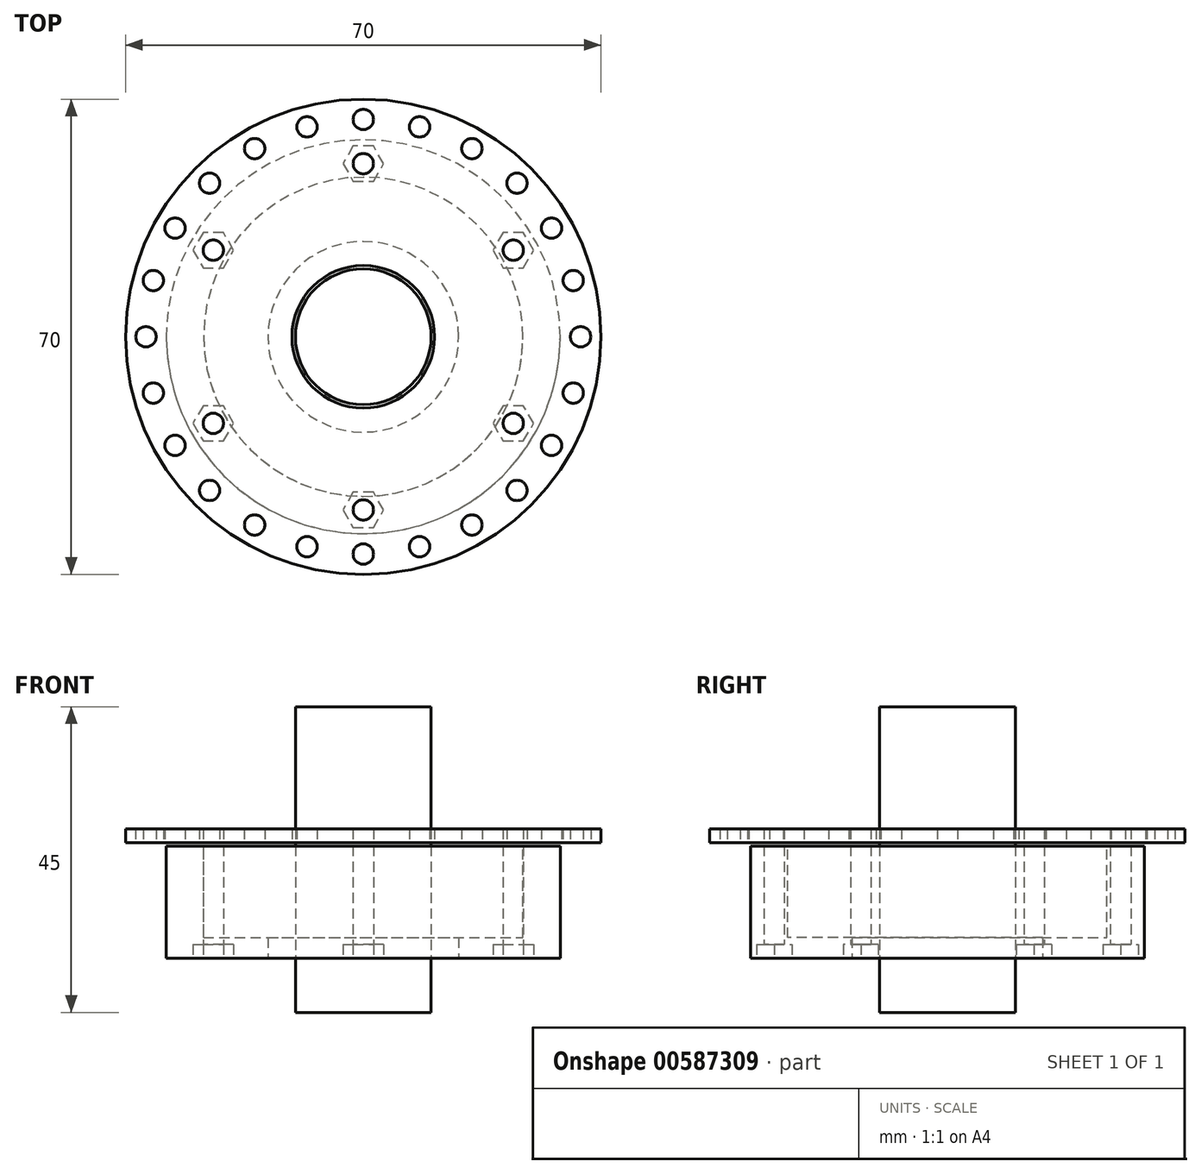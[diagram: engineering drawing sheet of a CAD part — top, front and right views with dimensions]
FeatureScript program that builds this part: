
annotation { "Feature Type Name" : "Feature", "Feature Type Description" : "" }
export const myFeature = defineFeature(function(context is Context, id is Id, definition is map)
    precondition{}
    {
        {
            var Q0;
            Q0=qCreatedBy(makeId("Top.planeOp"),FACE);
            var sketch = newSketch(context, id + "F0", { "sketchPlane" : qUnion([Q0]) });
            skCircle(sketch, "E0", {"center": v(0, 0) * mm, "radius": 10 * mm});
            skCircle(sketch, "E1", {"center": v(0, 0) * mm, "radius": 23.5 * mm});
            skCircle(sketch, "E2", {"center": v(0, 0) * mm, "radius": 19.54 * mm});
            skCircle(sketch, "E3", {"center": v(0, 0) * mm, "radius": 14.04 * mm});
            skSolve(sketch);
        }
        {
            var Q0;
            Q0=makeQuery(id+"F0.imprint","IMPRINT",FACE,{"disambiguationData":[TD([[makeQuery(id+"F0.imprint","IMPRINT",EDGE,{"derivedFrom":sQuery(id+"F0.wireOp",EDGE,"E2")}),1.0]])]});
            var Q1;
            Q1=makeQuery(id+"F0.imprint","IMPRINT",FACE,{"disambiguationData":[TD([[makeQuery(id+"F0.imprint","IMPRINT",EDGE,{"derivedFrom":sQuery(id+"F0.wireOp",EDGE,"E1")}),1.0]])]});
            var Q2;
            Q2=makeQuery(id+"F0.imprint","IMPRINT",FACE,{"disambiguationData":[TD([[makeQuery(id+"F0.imprint","IMPRINT",EDGE,{"derivedFrom":sQuery(id+"F0.wireOp",EDGE,"E0")}),-1.0]])]});
            extrude(context, id + "F1", {"entities" : qUnion([Q0, Q1, Q2]), "oppositeDirection" : true, "depth" : 14 * mm, "offsetDistance" : 25 * mm});
        }
        {
            var Q0;
            Q0=makeQuery(id+"F0.imprint","IMPRINT",FACE,{"disambiguationData":[TD([[makeQuery(id+"F0.imprint","IMPRINT",EDGE,{"derivedFrom":sQuery(id+"F0.wireOp",EDGE,"E2")}),1.0]])]});
            extrude(context, id + "F2", {"entities" : qUnion([Q0]), "operationType" : NewBodyOperationType.REMOVE, "oppositeDirection" : true, "depth" : 2 * mm, "offsetDistance" : 25 * mm});
        }
        {
            var Q0;
            Q0=makeQuery(id+"F1.opExtrude","CAP_EDGE",EDGE,{"disambiguationData":[OSD([sQuery(id+"F0.wireOp",EDGE,"E1")])],"isStart":true});
            var Q1;
            Q1=makeQuery(id+"F1.opExtrude","CAP_EDGE",EDGE,{"disambiguationData":[OSD([sQuery(id+"F0.wireOp",EDGE,"E1")])],"isStart":false});
            chamfer(context, id + "F3", {"entities" : qUnion([Q0, Q1]), "width" : 2 * mm, "tangentPropagation" : true});
        }
        {
            var Q0;
            Q0=makeQuery(id+"F1.opExtrude","CAP_EDGE",EDGE,{"disambiguationData":[OSD([sQuery(id+"F0.wireOp",EDGE,"E0")])],"isStart":false});
            var Q1;
            Q1=makeQuery(id+"F1.opExtrude","CAP_EDGE",EDGE,{"disambiguationData":[OSD([sQuery(id+"F0.wireOp",EDGE,"E0")])],"isStart":true});
            chamfer(context, id + "F4", {"entities" : qUnion([Q0, Q1]), "width" : 1 * mm, "tangentPropagation" : true});
        }
        {
            var Q0;
            Q0=makeQuery(id+"F1.opExtrude","CAP_FACE",FACE,{"disambiguationData":[OSD([sQuery(id+"F0.wireOp",EDGE,"E0"),sQuery(id+"F0.wireOp",EDGE,"E1")])],"isStart":false});
            var sketch = newSketch(context, id + "F5", { "sketchPlane" : qUnion([Q0]) });
            skCircle(sketch, "E4.0", {"center": v(0, 0) * mm, "radius": 14.04 * mm});
            skCircle(sketch, "E5.0", {"center": v(0, 0) * mm, "radius": 19.54 * mm});
            skSolve(sketch);
        }
        {
            var Q0;
            Q0 = qSketchRegion(id + "F5", true);
            extrude(context, id + "F6", {"entities" : qUnion([Q0]), "operationType" : NewBodyOperationType.REMOVE, "oppositeDirection" : true, "depth" : 2 * mm, "offsetDistance" : 25 * mm});
        }
        {
            var Q0;
            Q0=qCreatedBy(makeId("Top.planeOp"),FACE);
            var sketch = newSketch(context, id + "F7", { "sketchPlane" : qUnion([Q0]) });
            skCircle(sketch, "E6", {"center": v(0, 0) * mm, "radius": 35 * mm});
            skCircle(sketch, "E7", {"center": v(0, 32) * mm, "radius": 1.5 * mm});
            skCircle(sketch, "E8.1.0", {"center": v(-8.28, 30.9) * mm, "radius": 1.5 * mm});
            skCircle(sketch, "E8.2.0", {"center": v(-16, 27.71) * mm, "radius": 1.5 * mm});
            skCircle(sketch, "E8.3.0", {"center": v(-22.63, 22.63) * mm, "radius": 1.5 * mm});
            skCircle(sketch, "E8.4.0", {"center": v(-27.71, 16) * mm, "radius": 1.5 * mm});
            skCircle(sketch, "E8.5.0", {"center": v(-30.9, 8.28) * mm, "radius": 1.5 * mm});
            skCircle(sketch, "E8.6.0", {"center": v(-32, 0) * mm, "radius": 1.5 * mm});
            skCircle(sketch, "E8.7.0", {"center": v(-30.9, -8.28) * mm, "radius": 1.5 * mm});
            skCircle(sketch, "E8.8.0", {"center": v(-27.71, -16) * mm, "radius": 1.5 * mm});
            skCircle(sketch, "E8.9.0", {"center": v(-22.63, -22.63) * mm, "radius": 1.5 * mm});
            skCircle(sketch, "E8.10.0", {"center": v(-16, -27.71) * mm, "radius": 1.5 * mm});
            skCircle(sketch, "E8.11.0", {"center": v(-8.28, -30.9) * mm, "radius": 1.5 * mm});
            skCircle(sketch, "E8.12.0", {"center": v(0, -32) * mm, "radius": 1.5 * mm});
            skCircle(sketch, "E8.13.0", {"center": v(8.28, -30.9) * mm, "radius": 1.5 * mm});
            skCircle(sketch, "E8.14.0", {"center": v(16, -27.71) * mm, "radius": 1.5 * mm});
            skCircle(sketch, "E8.15.0", {"center": v(22.63, -22.63) * mm, "radius": 1.5 * mm});
            skCircle(sketch, "E8.16.0", {"center": v(27.71, -16) * mm, "radius": 1.5 * mm});
            skCircle(sketch, "E8.17.0", {"center": v(30.9, -8.28) * mm, "radius": 1.5 * mm});
            skCircle(sketch, "E8.18.0", {"center": v(32, 0) * mm, "radius": 1.5 * mm});
            skCircle(sketch, "E8.19.0", {"center": v(30.9, 8.28) * mm, "radius": 1.5 * mm});
            skCircle(sketch, "E8.20.0", {"center": v(27.71, 16) * mm, "radius": 1.5 * mm});
            skCircle(sketch, "E8.21.0", {"center": v(22.63, 22.63) * mm, "radius": 1.5 * mm});
            skCircle(sketch, "E8.22.0", {"center": v(16, 27.71) * mm, "radius": 1.5 * mm});
            skCircle(sketch, "E8.23.0", {"center": v(8.28, 30.9) * mm, "radius": 1.5 * mm});
            skCircle(sketch, "E9", {"center": v(0, 0) * mm, "radius": 10.5 * mm});
            skSolve(sketch);
        }
        {
            var Q0;
            Q0=makeQuery(id+"F7.imprint","IMPRINT",FACE,{"disambiguationData":[TD([[makeQuery(id+"F7.imprint","IMPRINT",EDGE,{"derivedFrom":sQuery(id+"F7.wireOp",EDGE,"E6")}),1.0]])]});
            extrude(context, id + "F8", {"entities" : qUnion([Q0]), "depth" : 2 * mm, "offsetDistance" : 25 * mm});
        }
        {
            var Q0;
            {var subQ0=sQuery(id+"F0.wireOp",EDGE,"E0");Q0=makeQuery(id+"F6.boolean.opBoolean","SPLIT",FACE,{"disambiguationData":[TD([makeQuery(id+"F6.opExtrude","SWEPT_FACE",FACE,{"disambiguationData":[OSD([sQuery(id+"F5.wireOp",EDGE,"E4.0")])]})])],"derivedFrom":makeQuery(id+"F1.opExtrude","CAP_FACE",FACE,{"disambiguationData":[OSD([subQ0,sQuery(id+"F0.wireOp",EDGE,"E1")])],"isStart":false})});}
            var sketch = newSketch(context, id + "F9", { "sketchPlane" : qUnion([Q0]) });
            skCircle(sketch, "E10", {"center": v(0, 0) * mm, "radius": 29 * mm});
            skCircle(sketch, "E11.0", {"center": v(0, 0) * mm, "radius": 10 * mm, "construction": true});
            skCircle(sketch, "E12", {"center": v(0, 0) * mm, "radius": 10.5 * mm});
            skSolve(sketch);
        }
        {
            var Q0;
            Q0=makeQuery(id+"F9.imprint","IMPRINT",FACE,{"disambiguationData":[TD([[makeQuery(id+"F9.imprint","IMPRINT",EDGE,{"derivedFrom":makeQuery(id+"F6.boolean.opBoolean","COPY",EDGE,{"derivedFrom":makeQuery(id+"F6.opExtrude","CAP_EDGE",EDGE,{"disambiguationData":[OSD([sQuery(id+"F5.wireOp",EDGE,"E4.0")])],"isStart":true})})}),-1.0]])]});
            var Q1;
            Q1=makeQuery(id+"F9.imprint","IMPRINT",FACE,{"disambiguationData":[TD([[makeQuery(id+"F9.imprint","IMPRINT",EDGE,{"derivedFrom":sQuery(id+"F9.wireOp",EDGE,"E10")}),1.0]])]});
            var Q2;
            Q2=makeQuery(id+"F8.opExtrude","CAP_FACE",FACE,{"disambiguationData":[OSD([sQuery(id+"F7.wireOp",EDGE,"E6"),sQuery(id+"F7.wireOp",EDGE,"E7"),sQuery(id+"F7.wireOp",EDGE,"E8.1.0"),sQuery(id+"F7.wireOp",EDGE,"E8.2.0"),sQuery(id+"F7.wireOp",EDGE,"E8.3.0"),sQuery(id+"F7.wireOp",EDGE,"E8.4.0"),sQuery(id+"F7.wireOp",EDGE,"E8.5.0"),sQuery(id+"F7.wireOp",EDGE,"E8.6.0"),sQuery(id+"F7.wireOp",EDGE,"E8.7.0"),sQuery(id+"F7.wireOp",EDGE,"E8.8.0"),sQuery(id+"F7.wireOp",EDGE,"E8.9.0"),sQuery(id+"F7.wireOp",EDGE,"E8.10.0"),sQuery(id+"F7.wireOp",EDGE,"E8.11.0"),sQuery(id+"F7.wireOp",EDGE,"E8.12.0"),sQuery(id+"F7.wireOp",EDGE,"E8.13.0"),sQuery(id+"F7.wireOp",EDGE,"E8.14.0"),sQuery(id+"F7.wireOp",EDGE,"E8.15.0"),sQuery(id+"F7.wireOp",EDGE,"E8.16.0"),sQuery(id+"F7.wireOp",EDGE,"E8.17.0"),sQuery(id+"F7.wireOp",EDGE,"E8.18.0"),sQuery(id+"F7.wireOp",EDGE,"E8.19.0"),sQuery(id+"F7.wireOp",EDGE,"E8.20.0"),sQuery(id+"F7.wireOp",EDGE,"E8.21.0"),sQuery(id+"F7.wireOp",EDGE,"E8.22.0"),sQuery(id+"F7.wireOp",EDGE,"E8.23.0"),sQuery(id+"F7.wireOp",EDGE,"E9"),sQuery(id+"F7.wireOp",EDGE,"SUpEN3Z2-evRc-ZjCU-vPrQ-KYs7HBq4r9Lc"),sQuery(id+"F7.wireOp",EDGE,"4f132e4c-be19-42d6-8573-d693d6a31837.1.0"),sQuery(id+"F7.wireOp",EDGE,"4f132e4c-be19-42d6-8573-d693d6a31837.2.0"),sQuery(id+"F7.wireOp",EDGE,"4f132e4c-be19-42d6-8573-d693d6a31837.3.0")])],"isStart":true});
            var Q3;
            Q3=makeQuery(id+"F8.opExtrude","SWEPT_BODY",BODY,{"disambiguationData":[OSD([sQuery(id+"F7.wireOp",EDGE,"E6"),sQuery(id+"F7.wireOp",EDGE,"E7"),sQuery(id+"F7.wireOp",EDGE,"E8.1.0"),sQuery(id+"F7.wireOp",EDGE,"E8.2.0"),sQuery(id+"F7.wireOp",EDGE,"E8.3.0"),sQuery(id+"F7.wireOp",EDGE,"E8.4.0"),sQuery(id+"F7.wireOp",EDGE,"E8.5.0"),sQuery(id+"F7.wireOp",EDGE,"E8.6.0"),sQuery(id+"F7.wireOp",EDGE,"E8.7.0"),sQuery(id+"F7.wireOp",EDGE,"E8.8.0"),sQuery(id+"F7.wireOp",EDGE,"E8.9.0"),sQuery(id+"F7.wireOp",EDGE,"E8.10.0"),sQuery(id+"F7.wireOp",EDGE,"E8.11.0"),sQuery(id+"F7.wireOp",EDGE,"E8.12.0"),sQuery(id+"F7.wireOp",EDGE,"E8.13.0"),sQuery(id+"F7.wireOp",EDGE,"E8.14.0"),sQuery(id+"F7.wireOp",EDGE,"E8.15.0"),sQuery(id+"F7.wireOp",EDGE,"E8.16.0"),sQuery(id+"F7.wireOp",EDGE,"E8.17.0"),sQuery(id+"F7.wireOp",EDGE,"E8.18.0"),sQuery(id+"F7.wireOp",EDGE,"E8.19.0"),sQuery(id+"F7.wireOp",EDGE,"E8.20.0"),sQuery(id+"F7.wireOp",EDGE,"E8.21.0"),sQuery(id+"F7.wireOp",EDGE,"E8.22.0"),sQuery(id+"F7.wireOp",EDGE,"E8.23.0"),sQuery(id+"F7.wireOp",EDGE,"E9"),sQuery(id+"F7.wireOp",EDGE,"SUpEN3Z2-evRc-ZjCU-vPrQ-KYs7HBq4r9Lc"),sQuery(id+"F7.wireOp",EDGE,"4f132e4c-be19-42d6-8573-d693d6a31837.1.0"),sQuery(id+"F7.wireOp",EDGE,"4f132e4c-be19-42d6-8573-d693d6a31837.2.0"),sQuery(id+"F7.wireOp",EDGE,"4f132e4c-be19-42d6-8573-d693d6a31837.3.0")])]});
            extrude(context, id + "F10", {"entities" : qUnion([Q0, Q1]), "endBound" : BoundingType.UP_TO_SURFACE, "oppositeDirection" : true, "depth" : 25 * mm, "endBoundEntityFace" : qUnion([Q2]), "endBoundEntityBody" : qUnion([Q3]), "hasOffset" : true, "offsetDistance" : 0.5 * mm, "hasSecondDirection" : true, "secondDirectionOppositeDirection" : false, "secondDirectionDepth" : 3 * mm});
        }
        {
            var Q0;
            Q0=makeQuery(id+"F0.imprint","IMPRINT",FACE,{"disambiguationData":[TD([[makeQuery(id+"F0.imprint","IMPRINT",EDGE,{"derivedFrom":sQuery(id+"F0.wireOp",EDGE,"E0")}),-1.0]])]});
            var Q1;
            Q1=makeQuery(id+"F0.imprint","IMPRINT",FACE,{"disambiguationData":[TD([[makeQuery(id+"F0.imprint","IMPRINT",EDGE,{"derivedFrom":sQuery(id+"F0.wireOp",EDGE,"E2")}),1.0]])]});
            var Q2;
            Q2=makeQuery(id+"F0.imprint","IMPRINT",FACE,{"disambiguationData":[TD([[makeQuery(id+"F0.imprint","IMPRINT",EDGE,{"derivedFrom":sQuery(id+"F0.wireOp",EDGE,"E1")}),1.0]])]});
            var Q3;
            Q3=makeQuery(id+"F10.opExtrude","CAP_FACE",FACE,{"disambiguationData":[OSD([sQuery(id+"F0.wireOp",EDGE,"E0"),sQuery(id+"F0.wireOp",EDGE,"E1"),sQuery(id+"F9.wireOp",EDGE,"E10")])],"isStart":true});
            extrude(context, id + "F11", {"entities" : qUnion([Q0, Q1, Q2]), "operationType" : NewBodyOperationType.REMOVE, "endBound" : BoundingType.UP_TO_SURFACE, "oppositeDirection" : true, "depth" : 25 * mm, "endBoundEntityFace" : qUnion([Q3]), "hasOffset" : true, "offsetDistance" : 3 * mm});
        }
        {
            var Q0;
            Q0=makeQuery(id+"F0.imprint","IMPRINT",FACE,{"disambiguationData":[TD([[makeQuery(id+"F0.imprint","IMPRINT",EDGE,{"derivedFrom":sQuery(id+"F0.wireOp",EDGE,"E0")}),1.0]])]});
            extrude(context, id + "F12", {"entities" : qUnion([Q0]), "depth" : 20 * mm, "offsetDistance" : 25 * mm, "hasSecondDirection" : true, "secondDirectionOppositeDirection" : true, "secondDirectionDepth" : 25 * mm});
        }
        {
            var Q0;
            Q0=makeQuery(id+"F10.opExtrude","CAP_FACE",FACE,{"disambiguationData":[OSD([sQuery(id+"F0.wireOp",EDGE,"E0"),sQuery(id+"F0.wireOp",EDGE,"E1"),sQuery(id+"F9.wireOp",EDGE,"E10")])],"isStart":true});
            var sketch = newSketch(context, id + "F13", { "sketchPlane" : qUnion([Q0]) });
            skCircle(sketch, "E13", {"center": v(0, 25.5) * mm, "radius": 1.5 * mm});
            skCircle(sketch, "E14.1.0", {"center": v(-22.08, 12.75) * mm, "radius": 1.5 * mm});
            skCircle(sketch, "E14.2.0", {"center": v(-22.08, -12.75) * mm, "radius": 1.5 * mm});
            skCircle(sketch, "E14.3.0", {"center": v(0, -25.5) * mm, "radius": 1.5 * mm});
            skPoint(sketch, "E14.center", {"position": v(0, 0) * mm});
            skCircle(sketch, "E15.0", {"center": v(0, 0) * mm, "radius": 23.5 * mm, "construction": true});
            skCircle(sketch, "E16.1.4.0", {"center": v(22.08, -12.75) * mm, "radius": 1.5 * mm});
            skCircle(sketch, "E16.1.5.0", {"center": v(22.08, 12.75) * mm, "radius": 1.5 * mm});
            skSolve(sketch);
        }
        {
            var Q0;
            Q0=makeQuery(id+"F13.imprint","IMPRINT",FACE,{"disambiguationData":[TD([[makeQuery(id+"F13.imprint","IMPRINT",EDGE,{"derivedFrom":sQuery(id+"F13.wireOp",EDGE,"E13")}),1.0]])]});
            var Q1;
            Q1=makeQuery(id+"F13.imprint","IMPRINT",FACE,{"disambiguationData":[TD([[makeQuery(id+"F13.imprint","IMPRINT",EDGE,{"derivedFrom":sQuery(id+"F13.wireOp",EDGE,"E14.1.0")}),1.0]])]});
            var Q2;
            Q2=makeQuery(id+"F13.imprint","IMPRINT",FACE,{"disambiguationData":[TD([[makeQuery(id+"F13.imprint","IMPRINT",EDGE,{"derivedFrom":sQuery(id+"F13.wireOp",EDGE,"E14.2.0")}),1.0]])]});
            var Q3;
            Q3=makeQuery(id+"F13.imprint","IMPRINT",FACE,{"disambiguationData":[TD([[makeQuery(id+"F13.imprint","IMPRINT",EDGE,{"derivedFrom":sQuery(id+"F13.wireOp",EDGE,"E14.3.0")}),1.0]])]});
            var Q4;
            Q4=makeQuery(id+"F13.imprint","IMPRINT",FACE,{"disambiguationData":[TD([[makeQuery(id+"F13.imprint","IMPRINT",EDGE,{"derivedFrom":sQuery(id+"F13.wireOp",EDGE,"E16.1.5.0")}),1.0]])]});
            var Q5;
            Q5=makeQuery(id+"F13.imprint","IMPRINT",FACE,{"disambiguationData":[TD([[makeQuery(id+"F13.imprint","IMPRINT",EDGE,{"derivedFrom":sQuery(id+"F13.wireOp",EDGE,"E16.1.4.0")}),1.0]])]});
            extrude(context, id + "F14", {"entities" : qUnion([Q0, Q1, Q2, Q3, Q4, Q5]), "operationType" : NewBodyOperationType.REMOVE, "endBound" : BoundingType.THROUGH_ALL, "oppositeDirection" : true, "depth" : 25 * mm, "offsetDistance" : 25 * mm});
        }
        {
            var Q0;
            Q0=makeQuery(id+"F10.opExtrude","CAP_FACE",FACE,{"disambiguationData":[OSD([sQuery(id+"F0.wireOp",EDGE,"E0"),sQuery(id+"F0.wireOp",EDGE,"E1"),sQuery(id+"F9.wireOp",EDGE,"E10")])],"isStart":true});
            var sketch = newSketch(context, id + "F15", { "sketchPlane" : qUnion([Q0]) });
            skCircle(sketch, "E17.cCircle", {"center": v(0, 25.5) * mm, "radius": 3 * mm, "construction": true});
            skLineSegment(sketch, "E17.0", {"start": v(1.5, 22.9) * mm, "end": v(-1.5, 22.9) * mm});
            skLineSegment(sketch, "E17.1", {"start": v(-1.5, 22.9) * mm, "end": v(-3, 25.5) * mm});
            skLineSegment(sketch, "E17.2", {"start": v(-3, 25.5) * mm, "end": v(-1.5, 28.1) * mm});
            skLineSegment(sketch, "E17.3", {"start": v(-1.5, 28.1) * mm, "end": v(1.5, 28.1) * mm});
            skLineSegment(sketch, "E17.4", {"start": v(1.5, 28.1) * mm, "end": v(3, 25.5) * mm});
            skLineSegment(sketch, "E17.5", {"start": v(3, 25.5) * mm, "end": v(1.5, 22.9) * mm});
            skLineSegment(sketch, "E18.1.0", {"start": v(-23.58, 10.15) * mm, "end": v(-25.08, 12.75) * mm});
            skLineSegment(sketch, "E18.1.1", {"start": v(-25.08, 12.75) * mm, "end": v(-23.58, 15.35) * mm});
            skLineSegment(sketch, "E18.1.2", {"start": v(-23.58, 15.35) * mm, "end": v(-20.58, 15.35) * mm});
            skLineSegment(sketch, "E18.1.3", {"start": v(-20.58, 15.35) * mm, "end": v(-19.08, 12.75) * mm});
            skLineSegment(sketch, "E18.1.4", {"start": v(-19.08, 12.75) * mm, "end": v(-20.58, 10.15) * mm});
            skLineSegment(sketch, "E18.1.5", {"start": v(-20.58, 10.15) * mm, "end": v(-23.58, 10.15) * mm});
            skLineSegment(sketch, "E18.2.0", {"start": v(-20.58, -15.35) * mm, "end": v(-23.58, -15.35) * mm});
            skLineSegment(sketch, "E18.2.1", {"start": v(-23.58, -15.35) * mm, "end": v(-25.08, -12.75) * mm});
            skLineSegment(sketch, "E18.2.2", {"start": v(-25.08, -12.75) * mm, "end": v(-23.58, -10.15) * mm});
            skLineSegment(sketch, "E18.2.3", {"start": v(-23.58, -10.15) * mm, "end": v(-20.58, -10.15) * mm});
            skLineSegment(sketch, "E18.2.4", {"start": v(-20.58, -10.15) * mm, "end": v(-19.08, -12.75) * mm});
            skLineSegment(sketch, "E18.2.5", {"start": v(-19.08, -12.75) * mm, "end": v(-20.58, -15.35) * mm});
            skLineSegment(sketch, "E18.3.0", {"start": v(3, -25.5) * mm, "end": v(1.5, -28.1) * mm});
            skLineSegment(sketch, "E18.3.1", {"start": v(1.5, -28.1) * mm, "end": v(-1.5, -28.1) * mm});
            skLineSegment(sketch, "E18.3.2", {"start": v(-1.5, -28.1) * mm, "end": v(-3, -25.5) * mm});
            skLineSegment(sketch, "E18.3.3", {"start": v(-3, -25.5) * mm, "end": v(-1.5, -22.9) * mm});
            skLineSegment(sketch, "E18.3.4", {"start": v(-1.5, -22.9) * mm, "end": v(1.5, -22.9) * mm});
            skLineSegment(sketch, "E18.3.5", {"start": v(1.5, -22.9) * mm, "end": v(3, -25.5) * mm});
            skLineSegment(sketch, "E18.4.0", {"start": v(23.58, -10.15) * mm, "end": v(25.08, -12.75) * mm});
            skLineSegment(sketch, "E18.4.1", {"start": v(25.08, -12.75) * mm, "end": v(23.58, -15.35) * mm});
            skLineSegment(sketch, "E18.4.2", {"start": v(23.58, -15.35) * mm, "end": v(20.58, -15.35) * mm});
            skLineSegment(sketch, "E18.4.3", {"start": v(20.58, -15.35) * mm, "end": v(19.08, -12.75) * mm});
            skLineSegment(sketch, "E18.4.4", {"start": v(19.08, -12.75) * mm, "end": v(20.58, -10.15) * mm});
            skLineSegment(sketch, "E18.4.5", {"start": v(20.58, -10.15) * mm, "end": v(23.58, -10.15) * mm});
            skLineSegment(sketch, "E18.5.0", {"start": v(20.58, 15.35) * mm, "end": v(23.58, 15.35) * mm});
            skLineSegment(sketch, "E18.5.1", {"start": v(23.58, 15.35) * mm, "end": v(25.08, 12.75) * mm});
            skLineSegment(sketch, "E18.5.2", {"start": v(25.08, 12.75) * mm, "end": v(23.58, 10.15) * mm});
            skLineSegment(sketch, "E18.5.3", {"start": v(23.58, 10.15) * mm, "end": v(20.58, 10.15) * mm});
            skLineSegment(sketch, "E18.5.4", {"start": v(20.58, 10.15) * mm, "end": v(19.08, 12.75) * mm});
            skLineSegment(sketch, "E18.5.5", {"start": v(19.08, 12.75) * mm, "end": v(20.58, 15.35) * mm});
            skPoint(sketch, "E18.center", {"position": v(0, 0) * mm});
            skSolve(sketch);
        }
        {
            var Q0;
            Q0=makeQuery(id+"F15.imprint","IMPRINT",FACE,{"disambiguationData":[TD([[makeQuery(id+"F15.imprint","IMPRINT",EDGE,{"derivedFrom":sQuery(id+"F15.wireOp",EDGE,"E17.0")}),-1.0]])]});
            var Q1;
            Q1=makeQuery(id+"F15.imprint","IMPRINT",FACE,{"disambiguationData":[TD([[makeQuery(id+"F15.imprint","IMPRINT",EDGE,{"derivedFrom":sQuery(id+"F15.wireOp",EDGE,"E18.1.0")}),-1.0]])]});
            var Q2;
            Q2=makeQuery(id+"F15.imprint","IMPRINT",FACE,{"disambiguationData":[TD([[makeQuery(id+"F15.imprint","IMPRINT",EDGE,{"derivedFrom":sQuery(id+"F15.wireOp",EDGE,"E18.2.0")}),-1.0]])]});
            var Q3;
            Q3=makeQuery(id+"F15.imprint","IMPRINT",FACE,{"disambiguationData":[TD([[makeQuery(id+"F15.imprint","IMPRINT",EDGE,{"derivedFrom":sQuery(id+"F15.wireOp",EDGE,"E18.5.0")}),-1.0]])]});
            var Q4;
            Q4=makeQuery(id+"F15.imprint","IMPRINT",FACE,{"disambiguationData":[TD([[makeQuery(id+"F15.imprint","IMPRINT",EDGE,{"derivedFrom":sQuery(id+"F15.wireOp",EDGE,"E18.4.0")}),-1.0]])]});
            var Q5;
            Q5=makeQuery(id+"F15.imprint","IMPRINT",FACE,{"disambiguationData":[TD([[makeQuery(id+"F15.imprint","IMPRINT",EDGE,{"derivedFrom":sQuery(id+"F15.wireOp",EDGE,"E18.3.0")}),-1.0]])]});
            extrude(context, id + "F16", {"entities" : qUnion([Q0, Q1, Q2, Q3, Q4, Q5]), "operationType" : NewBodyOperationType.REMOVE, "oppositeDirection" : true, "depth" : 2 * mm, "offsetDistance" : 25 * mm});
        }
    });
